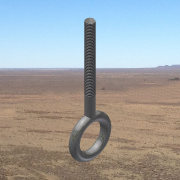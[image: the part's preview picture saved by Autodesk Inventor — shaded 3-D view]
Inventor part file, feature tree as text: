
AUTODESK INVENTOR PART (.ipt)
format: ipt  version: 2013 SP2 (Build 170200200, 200)  size: 162,304 bytes
history: native  units: in
note: dims shown in document units (in); Inventor stores cm internally (conversion verified against a paired STEP export)
features: sketch x3, plane x2, extrude x1, thread x1, revolve x1
ambient origin geometry x8: Origin, YZ Plane, XZ Plane, XY Plane, X Axis, Y Axis, Z Axis, Center Point
bodies: Solid1 (feature_tree)
feature tree (8):
  extrude  "Extrusion1"  Depth=4.0in TaperAngle=0.0deg
  thread  "Thread4"  [1 undecoded]
  sketch  "Sketch2"  dims[d15=-0.1875in d17=0.375in]
  plane  "Work Plane1"
  plane  "Work Plane2"
  revolve  "Revolution1"  [1 undecoded]
  sketch  "Sketch1"  dims[d0=0.375in d2=4.0in d3=0.0in d10=3.0in d11=0.0in]
  sketch  "Sketch5"  dims[d18=0.75in d19=90.0deg]
note: 2 required parameter values undecoded (feature->parameter linkage not recoverable at this tier; creation-order binding heuristic only, values carry confidence <= 0.55)